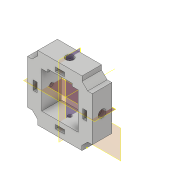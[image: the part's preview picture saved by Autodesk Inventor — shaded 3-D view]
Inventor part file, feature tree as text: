
AUTODESK INVENTOR PART (.ipt)
format: ipt  version: 2022 (Build 260153000, 153)  size: 317,952 bytes
history: native  units: mm
features: plane x7, extrude x5, sketch x5, projected_geometry x4, pattern_circular x2, hole x1, other x1
ambient origin geometry x8: Origin, YZ Plane, XZ Plane, XY Plane, X Axis, Y Axis, Z Axis, Center Point
bodies: Body1 (feature_tree)
feature tree (25):
  plane  "Work Plane5"
  extrude  "Extrusion1"  Depth=15.0mm
  extrude  "IM_offset"  Depth=53.8mm
  extrude  "Extrusion23"  Depth=45.0mm
  plane  "Arbeitsebene7"
  plane  "Arbeitsebene8"
  plane  "Arbeitsebene9"
  plane  "Arbeitsebene10"
  hole  "Bohrung2"  [1 undecoded]
  other  "Arbeitsachse1"
  pattern_circular  "Runde Anordnung2"  [2 undecoded]
  plane  "Arbeitsebene11"
  plane  "Arbeitsebene12"
  sketch  "Sketch31"  dims[d21=45.0mm d22=45.0mm]
  extrude  "Extrusion25"  Depth=7.0mm
  pattern_circular  "Circular Pattern3"  [2 undecoded]
  extrude  "Extrusion26"  Depth=7.0mm
  sketch  "Sketch1"  dims[d10=15.0mm d11=0.0mm d18=53.8mm]
  sketch  "Skizze4"  dims[d19=45.0deg d20=53.8mm]
  projected_geometry  "Projizierte Kontur1"
  projected_geometry  "Projizierte Kontur18"
  sketch  "Sketch32"  dims[d30=20.0mm d31=20.0mm]
  projected_geometry  "Projected Loop19"
  sketch  "Sketch33"  dims[d32=2.8mm d33=2.8mm d34=2.8mm d35=3.0mm d36=0.1mm d37=0.1mm d38=0.1mm d39=0.1mm d40=0.2mm d41=10.0mm d42=0.0mm d172=10.0mm d173=0.0mm d177=2.8mm d178=6.0mm d179=6.0mm d180=3.0mm d181=90.0deg d182=8.0mm d183=20.594885mm d184=40.0mm d185=360.0deg d188=0.1mm d189=0.1mm d190=3.0mm d191=7.0mm d192=0.0mm d193=0.0mm d194=40.0mm d195=360.0deg d197=0.0mm d198=0.0mm]
  projected_geometry  "Projected Loop20"
note: 5 required parameter values undecoded (feature->parameter linkage not recoverable at this tier; creation-order binding heuristic only, values carry confidence <= 0.55)
